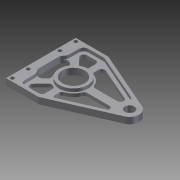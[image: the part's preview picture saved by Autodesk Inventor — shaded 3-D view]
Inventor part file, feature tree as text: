
AUTODESK INVENTOR PART (.ipt)
format: ipt  version: 2012 (Build 160160000, 160)  size: 280,576 bytes
history: native  units: in
note: dims shown in document units (in); Inventor stores cm internally (conversion verified against a paired STEP export)
features: extrude x3, fillet x3, sketch x2, hole x1
ambient origin geometry x8: Origin, YZ Plane, XZ Plane, XY Plane, X Axis, Y Axis, Z Axis, Center Point
bodies: Solid1 (feature_tree)
feature tree (9):
  sketch  "Sketch1"  dims[d0=2.75in d1=3.5in]
  extrude  "Extrusion1"  Depth=3.5in
  extrude  "Extrusion2"  Depth=0.1621in
  fillet  "Fillet1"  Radius=0.375in
  hole  "Hole1"  [1 undecoded]
  sketch  "Sketch2"  dims[d2=1.375in d6=0.1621in d7=0.375in d8=1.289in d9=0.875in d10=0.125in d11=0.0in d12=0.625in d13=0.1562in d14=0.1562in d15=0.25in d16=0.25in d17=0.125in d18=0.125in d19=0.125in d20=0.125in d21=0.125in d22=0.125in d24=0.125in d25=0.125in d26=0.25in d27=0.3125in d28=0.25in d29=0.125in d30=0.0in d31=0.125in d32=0.125in d33=0.125in d35=0.125in d36=0.125in d38=0.144in d39=0.75in d40=0.25in d41=0.25in d42=0.5635in d43=1.0in d44=0.8108in d45=0.4375in d46=0.125in d47=0.125in d48=0.125in d49=0.125in d51=0.125in d53=0.875in d54=0.0625in d58=0.125in d59=0.0in d62=0.75in d63=0.75in d69=0.125in d70=0.1621in d71=0.375in d72=1.125in d73=0.1875in d75=0.25in]
  extrude  "Extrusion4"  Depth=0.875in
  fillet  "Fillet6"  Radius=0.125in
  fillet  "Fillet8"  Radius=0.625in
note: 1 required parameter value undecoded (feature->parameter linkage not recoverable at this tier; creation-order binding heuristic only, values carry confidence <= 0.55)
